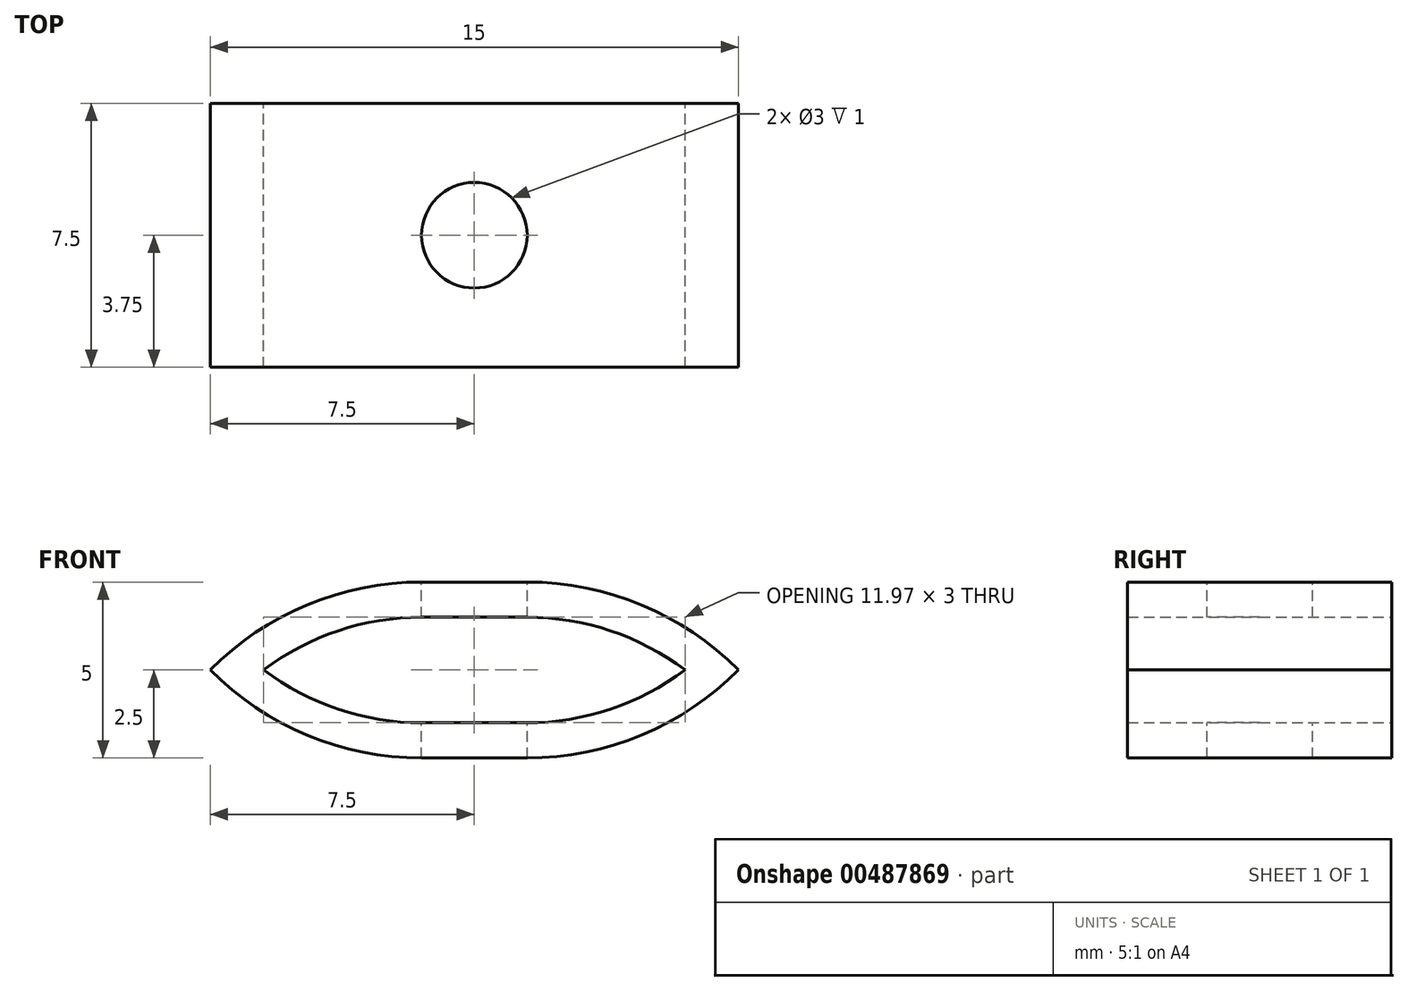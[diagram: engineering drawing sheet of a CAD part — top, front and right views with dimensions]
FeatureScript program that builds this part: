
annotation { "Feature Type Name" : "Feature", "Feature Type Description" : "" }
export const myFeature = defineFeature(function(context is Context, id is Id, definition is map)
    precondition{}
    {
        {
            var Q0;
            Q0=qCreatedBy(makeId("Front.planeOp"),FACE);
            var sketch = newSketch(context, id + "F0", { "sketchPlane" : qUnion([Q0])});
            skLineSegment(sketch, "E0.bottom", {"start": v(1.5, 1.5) * mm, "end": v(-1.5, 1.5) * mm});
            skLineSegment(sketch, "E0.top", {"start": v(1.5, -1.5) * mm, "end": v(-1.5, -1.5) * mm});
            skLineSegment(sketch, "E0.left", {"start": v(1.5, 1.5) * mm, "end": v(1.5, -1.5) * mm, "construction": true});
            skLineSegment(sketch, "E0.right", {"start": v(-1.5, 1.5) * mm, "end": v(-1.5, -1.5) * mm, "construction": true});
            skPoint(sketch, "E0.middle", {"position": v(0, 0) * mm});
            skLineSegment(sketch, "E1", {"start": v(1.5, 1.5) * mm, "end": v(1.5, 2.5) * mm, "construction": true});
            skLineSegment(sketch, "E2", {"start": v(-1.5, -1.5) * mm, "end": v(-1.5, -2.5) * mm, "construction": true});
            skLineSegment(sketch, "E3", {"start": v(1.5, 2.5) * mm, "end": v(-1.5, 2.5) * mm});
            skLineSegment(sketch, "E4", {"start": v(-1.5, -2.5) * mm, "end": v(1.5, -2.5) * mm});
            skArc(sketch, "E5", {"start": v(1.5, 2.5) * mm, "mid": v(4.75, 1.85) * mm, "end": v(7.5, 0) * mm});
            skArc(sketch, "E6", {"start": v(1.5, 1.5) * mm, "mid": v(3.86, 1.12) * mm, "end": v(5.98, 0) * mm});
            skArc(sketch, "E7", {"start": v(1.5, -1.5) * mm, "mid": v(3.86, -1.12) * mm, "end": v(5.98, 0) * mm});
            skArc(sketch, "E8", {"start": v(1.5, -2.5) * mm, "mid": v(4.75, -1.85) * mm, "end": v(7.5, 0) * mm});
            skArc(sketch, "E9", {"start": v(-1.5, -2.5) * mm, "mid": v(-4.75, -1.85) * mm, "end": v(-7.5, 0) * mm});
            skArc(sketch, "E10", {"start": v(-1.5, -1.5) * mm, "mid": v(-3.86, -1.12) * mm, "end": v(-5.98, 0) * mm});
            skArc(sketch, "E11", {"start": v(-1.5, 1.5) * mm, "mid": v(-3.86, 1.12) * mm, "end": v(-5.98, 0) * mm});
            skArc(sketch, "E12", {"start": v(-1.5, 2.5) * mm, "mid": v(-4.75, 1.85) * mm, "end": v(-7.5, 0) * mm});
            skSolve(sketch);
        }
        {
            var Q0;
            Q0 = qSketchRegion(id + "F0", true);
            extrude(context, id + "F1", {"entities" : qUnion([Q0]), "depth" : 7.5 * mm, "offsetDistance" : 25 * mm});
        }
        {
            var Q0;
            Q0=makeQuery(id+"F1.opExtrude","SWEPT_FACE",FACE,{"disambiguationData":[OSD([sQuery(id+"F0.wireOp",EDGE,"E3")])]});
            var sketch = newSketch(context, id + "F2", { "sketchPlane" : qUnion([Q0])});
            skLineSegment(sketch, "E13", {"start": v(-1.5, 0) * mm, "end": v(1.5, -7.5) * mm, "construction": true});
            skCircle(sketch, "E14", {"center": v(0, -3.75) * mm, "radius": 1.5 * mm});
            skSolve(sketch);
        }
        {
            var Q0;
            Q0 = qSketchRegion(id + "F2", true);
            extrude(context, id + "F3", {"entities" : qUnion([Q0]), "operationType" : NewBodyOperationType.REMOVE, "endBound" : BoundingType.THROUGH_ALL, "oppositeDirection" : true, "depth" : 25 * mm, "offsetDistance" : 25 * mm});
        }
    });
